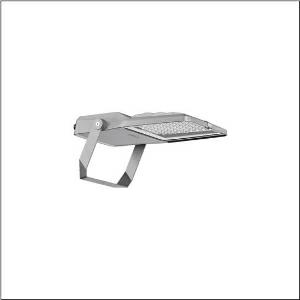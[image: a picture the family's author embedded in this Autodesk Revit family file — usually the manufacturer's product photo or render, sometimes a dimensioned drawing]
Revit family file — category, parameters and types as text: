
# Revit family: floodlight_fl_21_mini___pl52_5xa7771c2d1a_a6f7
name_source: partatom
category: Lighting Fixtures
units: mm (PartAtom-declared; Revit-internal decimal feet)

## family parameters
Cut with Voids When Loaded = No
Host = Face
Light Source = No
Part Type = Normal
Room Calculation Point = No
Round Connector Dimension = Use Diameter
Shared = No

## types (1)
- --- (1 x LED, 12210 lm, 87.2 W, 3000K)
    Apparent Load = 87 VA
    CIE Flux Codes = 26 60 98 100 100
    Color Rendering = 70
    Color Temperature = 3000K
    Default Elevation = 1800 mm
    Description = Floodlight FL 21 mini, floodlight, primary light control with lens, of PMMA, primary optical cover: protective disc, of toughened safety glass, transparent, light distribution: PL52, light emission: direct distribution, installation type: surface-mounted, LED, High Power LED, rated luminous flux: 12.210lm, luminous efficacy: 140lm/W, light colour: 730, colour temperature: 3000K, control gear: ECG iQ, control: Auto-Match, Temp-Guard, Lumen-Switch, Night-Set, Smart-Wire, Light-Fading, Desk-Remote (wireless, voltage-free reading and setting of iQ features in the workshop via application-optimized NFC function/RFID function), optimised constant luminous flux control (CLO 2.0), with terminal, 6-pole, mains connection: 220..240V, AC, 50/60Hz, start of lifetime: 87W, end of lifetime: 92W, reduction: 40W, luminaire housing, of diecast aluminium, powder-coated, Siteco® metallic grey (DB 702S), corrosivity category C5 according to DIN EN ISO 12944, mounting bracket, of steel, galvanised, powder-coated, Siteco® metallic grey (DB 702S), protection rating (complete): IP66, insulation class (complete): insulation class II (safety insulation), certification: CE, ENEC, VDE, protection symbol: D, impact resistance: IK08, permissible operating ambient temperature: -40..+40°C, permissible operating ambient temperature for outdoor applications: -40..+50°C, standard: DIN EN 12944, packaging unit: 1 piece

Light Distribution: PL52
    Height = 70 mm
    Lamp = 1 x LED
    Lamp Light Flux = 12210 lm
    Lamp Power = 87.2 W
    Lamp count = 1
    Length = 485 mm
    Luminous efficacy = 140 lm/W
    Manufacturer = Siteco
    ModVariant = No
    Model = 5XA7771C2D1A
    Number of Poles = 1
    OnlyDefault = Yes
    Power Factor = 1
    Product Name = Floodlight FL 21 mini | PL52
    Product group = floodlight | pylon top
    ProductGroupID = 6101
    Protection Class = Protection class II
    Protection Degree = IP 66
    RLX_Detail_Level = 1
    RlxData = <blob elided: 96249 chars, md5=ac336e05>
    Socket = socket
    Standby Power = 0 W
    System Light Flux = 12210 lm
    System Power = 87 W
    Type Comments = factory setting: luminous flux: 100 % | dim-lin: 254 | 456 mA
    Type Image = l_1006845.jpg
    URL = http://relux.com
    VarID = @adj_075747
    Voltage = 0 V
    Weight = 0.00 kg
    Width = 337 mm

## geometry (parser evidence)
native form markers: Blend x4, Sweep x14
no freeform markers — native parametric forms only
